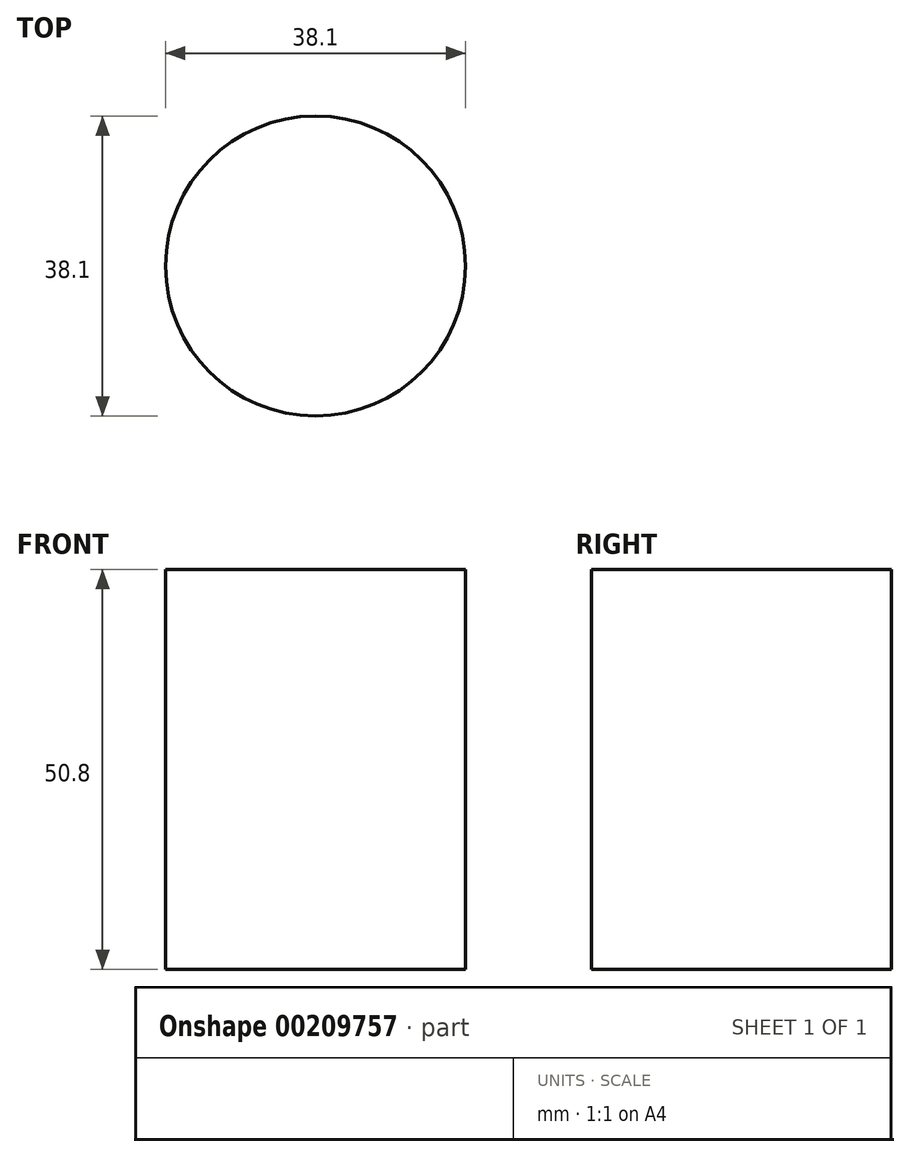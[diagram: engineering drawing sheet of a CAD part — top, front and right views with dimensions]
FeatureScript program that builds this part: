
annotation { "Feature Type Name" : "Feature", "Feature Type Description" : "" }
export const myFeature = defineFeature(function(context is Context, id is Id, definition is map)
    precondition{}
    {
        {
            var Q0;
            Q0=qCreatedBy(makeId("Front.planeOp"),FACE);
            var sketch = newSketch(context, id + "F0", { "sketchPlane" : qUnion([Q0])});
            skLineSegment(sketch, "E0.bottom", {"start": v(0, 0) * mm, "end": v(19.05, 0) * mm});
            skLineSegment(sketch, "E0.top", {"start": v(0, 50.8) * mm, "end": v(19.05, 50.8) * mm});
            skLineSegment(sketch, "E0.left", {"start": v(0, 0) * mm, "end": v(0, 50.8) * mm});
            skLineSegment(sketch, "E0.right", {"start": v(19.05, 0) * mm, "end": v(19.05, 50.8) * mm});
            skSolve(sketch);
        }
        {
            var Q0;
            Q0 = qSketchRegion(id + "F0", true);
            var Q1;
            Q1=sQuery(id+"F0.wireOp",EDGE,"E0.left");
            revolve(context, id + "F1", {"entities" : qUnion([Q0]), "axis" : qUnion([Q1]), "revolveType" : RevolveType.FULL});
        }
    });
